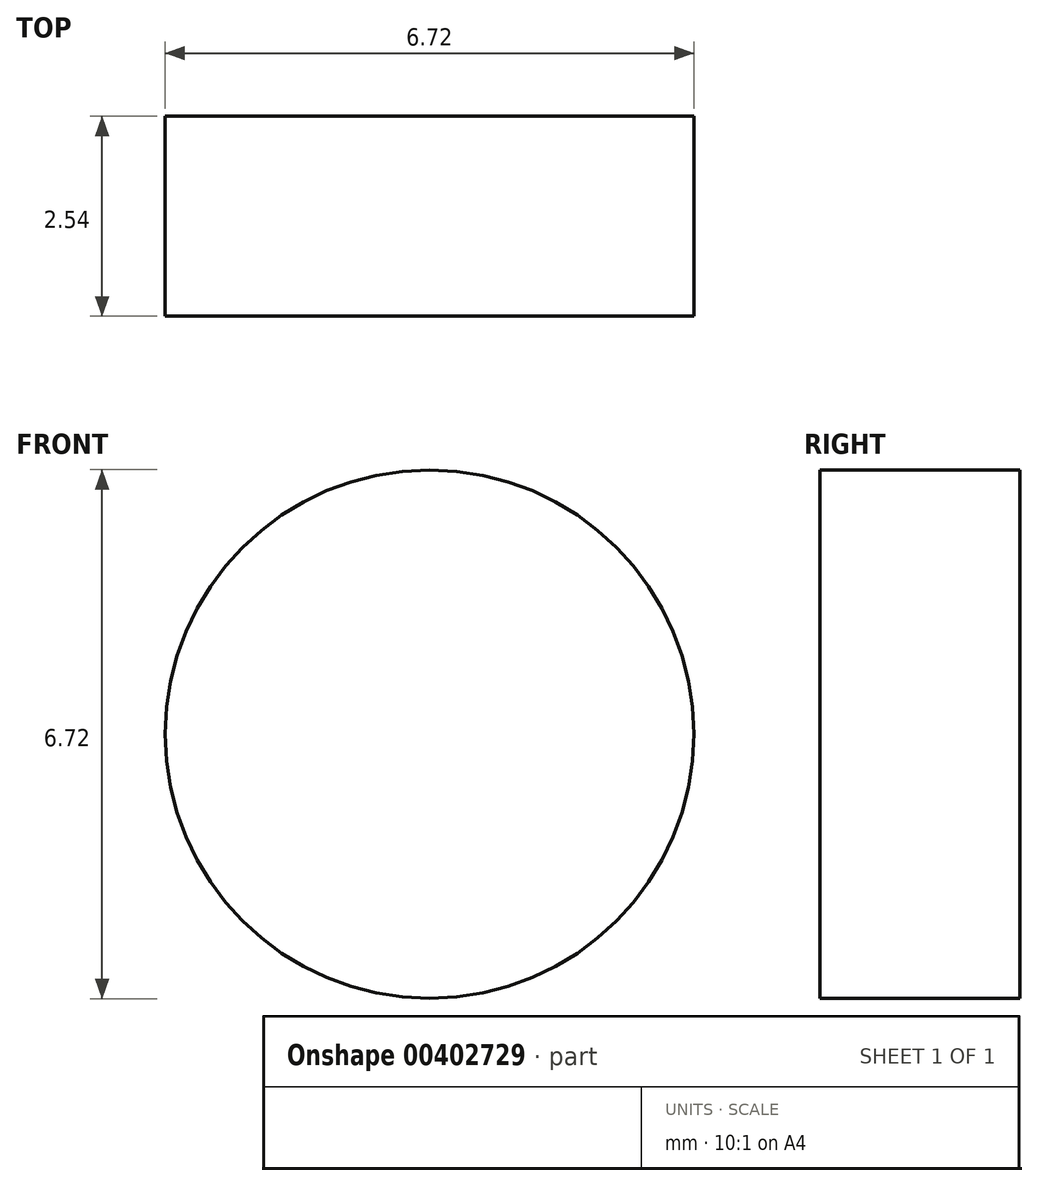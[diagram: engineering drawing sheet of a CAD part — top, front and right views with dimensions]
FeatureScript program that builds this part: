
annotation { "Feature Type Name" : "Feature", "Feature Type Description" : "" }
export const myFeature = defineFeature(function(context is Context, id is Id, definition is map)
    precondition{}
    {
        {
            var Q0;
            Q0=qCreatedBy(makeId("Front.planeOp"),FACE);
            var sketch = newSketch(context, id + "F0", { "sketchPlane" : qUnion([Q0])});
            skCircle(sketch, "E0", {"center": v(0, 0) * mm, "radius": 3.36 * mm});
            skSolve(sketch);
        }
        {
            var Q0;
            Q0 = qSketchRegion(id + "F0", true);
            extrude(context, id + "F1", {"entities" : qUnion([Q0]), "depth" : 2.54 * mm});
        }
    });
